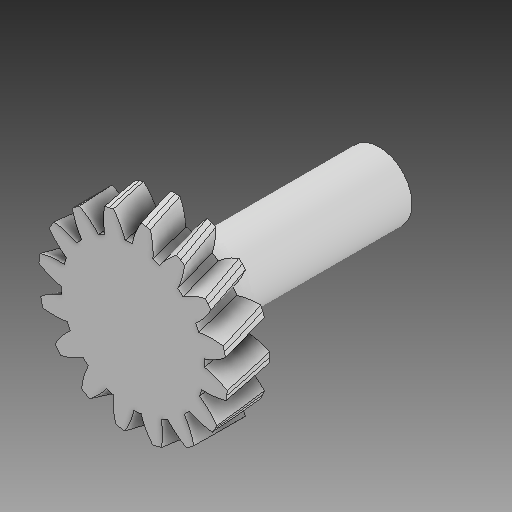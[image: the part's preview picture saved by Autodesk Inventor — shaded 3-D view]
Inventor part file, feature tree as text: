
AUTODESK INVENTOR PART (.ipt)
format: ipt  version: 2020 (Build 240168000, 168)  size: 449,536 bytes
history: native  units: mm
features: other x2, sketch x2, revolve x1, extrude x1
ambient origin geometry x8: Origin, YZ Plane, XZ Plane, XY Plane, X Axis, Y Axis, Z Axis, Center Point
bodies: Solid1 (feature_tree)
feature tree (6):
  revolve  "Revolution1"  [1 undecoded]
  other  "Spur Gear Teeth1"
  extrude  "Extrusion1"  Depth=22.0mm
  sketch  "Sketch1"  dims[d0=3.9mm d1=2.0mm]
  other  "Spur Gear1"
  sketch  "Sketch2"  dims[d2=1.0mm d3=22.0mm d4=5.0mm d5=15.0mm d7=90.0deg d8=6.45mm d9=3.0mm d10=0.0mm]
note: 1 required parameter value undecoded (feature->parameter linkage not recoverable at this tier; creation-order binding heuristic only, values carry confidence <= 0.55)
